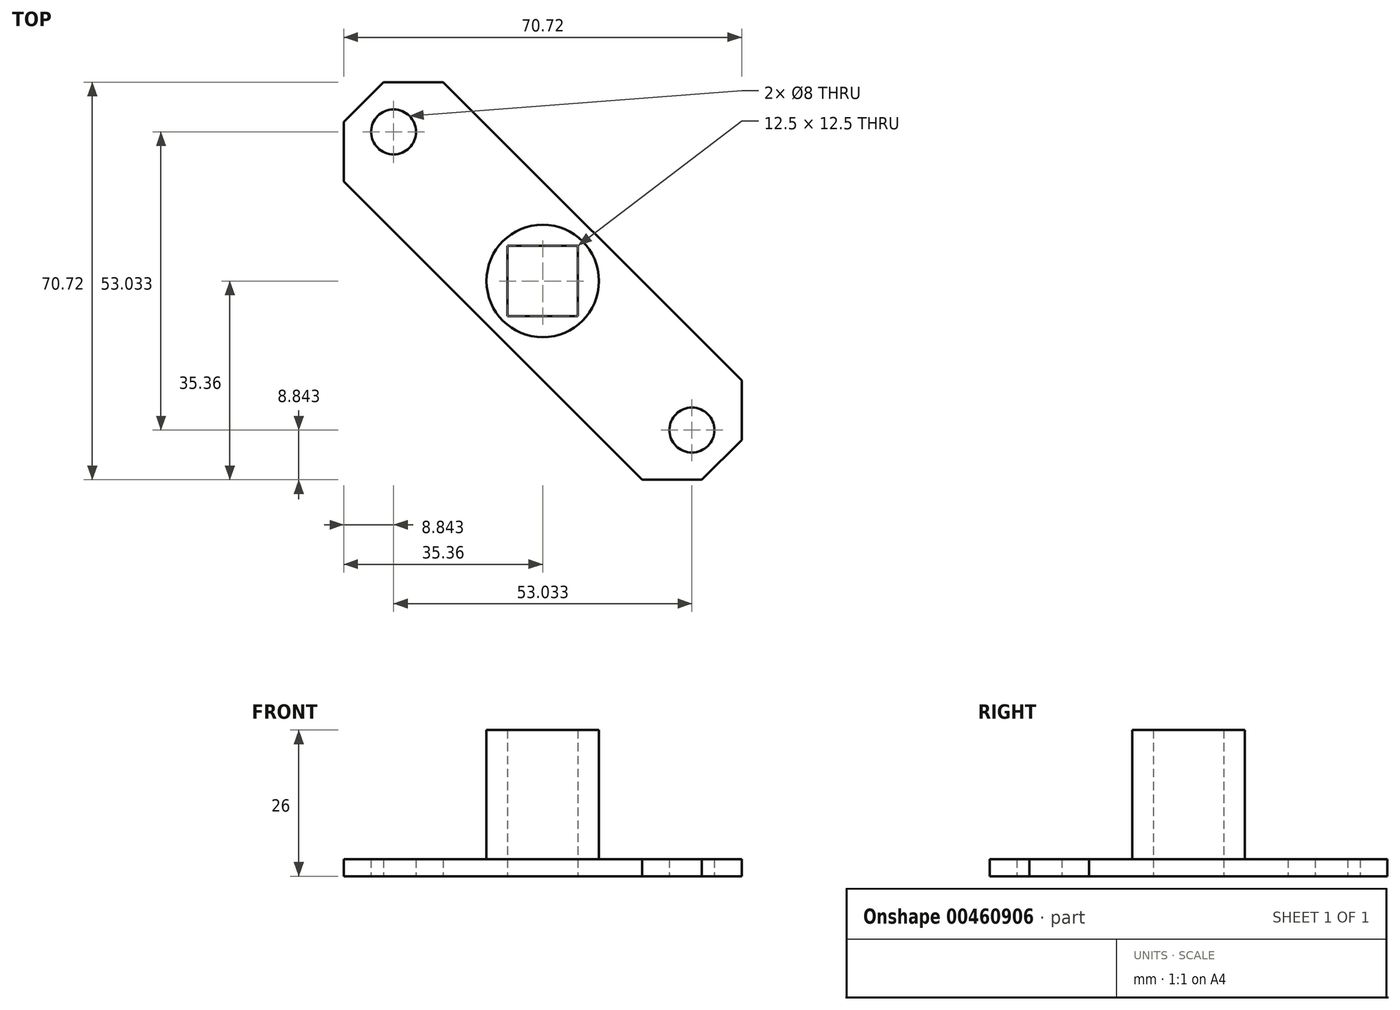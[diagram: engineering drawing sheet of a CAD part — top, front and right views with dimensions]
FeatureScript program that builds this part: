
annotation { "Feature Type Name" : "Feature", "Feature Type Description" : "" }
export const myFeature = defineFeature(function(context is Context, id is Id, definition is map)
    precondition{}
    {
        {
            var Q0;
            Q0=qCreatedBy(makeId("Top.planeOp"),FACE);
            var sketch = newSketch(context, id + "F0", { "sketchPlane" : qUnion([Q0])});
            skLineSegment(sketch, "E0", {"start": v(-28.28, 35.36) * mm, "end": v(-17.68, 35.36) * mm});
            skLineSegment(sketch, "E1", {"start": v(-17.68, 35.36) * mm, "end": v(35.36, -17.68) * mm});
            skLineSegment(sketch, "E2", {"start": v(35.36, -17.68) * mm, "end": v(35.36, -28.28) * mm});
            skLineSegment(sketch, "E3", {"start": v(35.36, -28.28) * mm, "end": v(28.28, -35.36) * mm});
            skLineSegment(sketch, "E4", {"start": v(28.28, -35.36) * mm, "end": v(17.68, -35.36) * mm});
            skLineSegment(sketch, "E5", {"start": v(17.68, -35.36) * mm, "end": v(-35.36, 17.68) * mm});
            skLineSegment(sketch, "E6", {"start": v(-35.36, 17.68) * mm, "end": v(-35.36, 28.28) * mm});
            skLineSegment(sketch, "E7", {"start": v(-35.36, 28.28) * mm, "end": v(-28.28, 35.36) * mm});
            skLineSegment(sketch, "E8", {"start": v(-17.68, 35.36) * mm, "end": v(17.68, -35.36) * mm, "construction": true});
            skLineSegment(sketch, "E9", {"start": v(-35.36, 17.68) * mm, "end": v(35.36, -17.68) * mm, "construction": true});
            skLineSegment(sketch, "E10", {"start": v(-17.68, 35.36) * mm, "end": v(-35.36, 17.68) * mm, "construction": true});
            skLineSegment(sketch, "E11", {"start": v(35.36, -17.68) * mm, "end": v(17.68, -35.36) * mm, "construction": true});
            skCircle(sketch, "E12", {"center": v(-26.52, 26.52) * mm, "radius": 4 * mm});
            skCircle(sketch, "E13", {"center": v(26.52, -26.52) * mm, "radius": 4 * mm});
            skCircle(sketch, "E14", {"center": v(0, 0) * mm, "radius": 10 * mm});
            skLineSegment(sketch, "E15.bottom", {"start": v(6.25, 6.25) * mm, "end": v(-6.25, 6.25) * mm});
            skLineSegment(sketch, "E15.top", {"start": v(6.25, -6.25) * mm, "end": v(-6.25, -6.25) * mm});
            skLineSegment(sketch, "E15.left", {"start": v(6.25, 6.25) * mm, "end": v(6.25, -6.25) * mm});
            skLineSegment(sketch, "E15.right", {"start": v(-6.25, 6.25) * mm, "end": v(-6.25, -6.25) * mm});
            skSolve(sketch);
        }
        {
            var Q0;
            Q0=makeQuery(id+"F0.imprint","IMPRINT",FACE,{"disambiguationData":[TD([[makeQuery(id+"F0.imprint","IMPRINT",EDGE,{"derivedFrom":sQuery(id+"F0.wireOp",EDGE,"E0")}),-1.0]])]});
            var Q1;
            Q1=makeQuery(id+"F0.imprint","IMPRINT",FACE,{"disambiguationData":[TD([[makeQuery(id+"F0.imprint","IMPRINT",EDGE,{"derivedFrom":sQuery(id+"F0.wireOp",EDGE,"E14")}),1.0]])]});
            extrude(context, id + "F1", {"entities" : qUnion([Q0, Q1]), "depth" : 3 * mm, "offsetDistance" : 25 * mm});
        }
        {
            var Q0;
            Q0=makeQuery(id+"F0.imprint","IMPRINT",FACE,{"disambiguationData":[TD([[makeQuery(id+"F0.imprint","IMPRINT",EDGE,{"derivedFrom":sQuery(id+"F0.wireOp",EDGE,"E14")}),1.0]])]});
            extrude(context, id + "F2", {"entities" : qUnion([Q0]), "operationType" : NewBodyOperationType.ADD, "depth" : 26 * mm, "offsetDistance" : 25 * mm});
        }
    });
